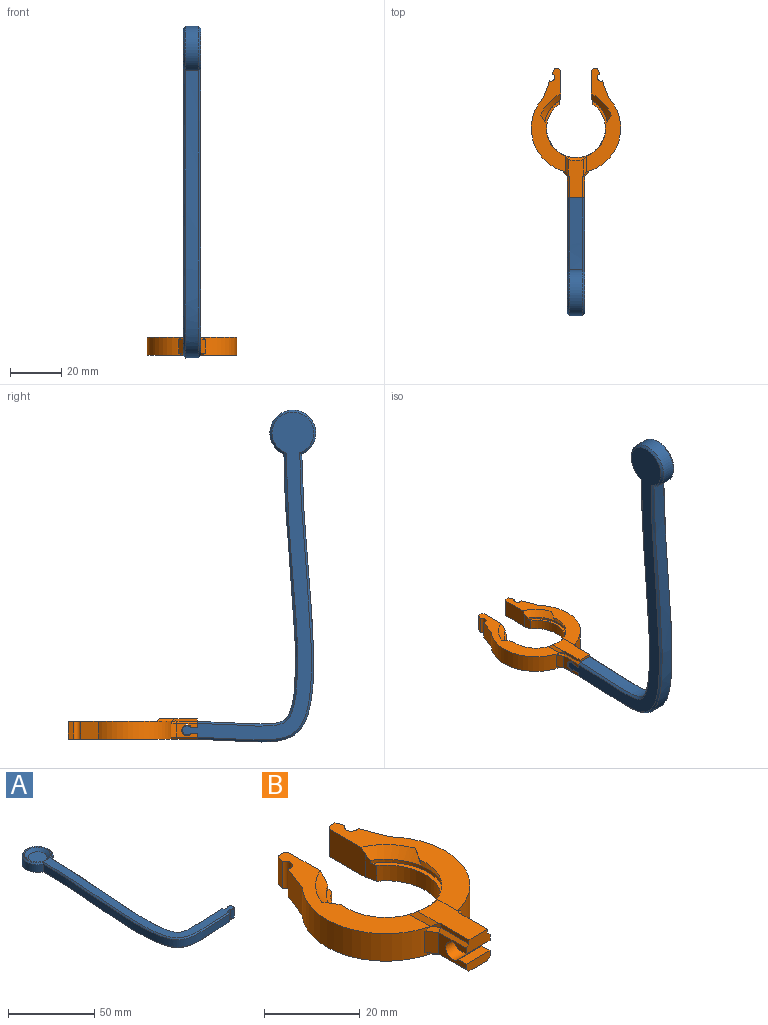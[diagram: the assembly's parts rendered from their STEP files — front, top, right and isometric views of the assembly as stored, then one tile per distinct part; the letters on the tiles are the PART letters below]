
ASSEMBLY  parts=2 mates=1
PART A: 20 faces, bbox 54x130.1x7 mm
  f0: plane 7x2.3mm, normal (1,0,0), area 15.5mm2, adj f1,f7,f8,f9,f11,f14
  f1: plane 7.01x2.67mm, normal (0,-1,0), area 16.9mm2, adj f0,f2,f8,f9,f18,f19
  f2: cylinder r=2mm len=6.6mm, axis (0,0,-1), area 65.9mm2, adj f1,f3,f18,f19
  f3: plane 7.01x2.67mm, normal (0,1,0), area 16.9mm2, adj f2,f4,f8,f9,f18,f19
  f4: plane 7x2.3mm, normal (1,0,0), area 15.5mm2, adj f3,f5,f8,f9,f10,f13
  f5: extruded ~105.77x38.57mm, area 753.8mm2, adj f4,f6,f10,f13
  f6: cylinder r=9mm len=18mm, axis (0,0,-1), area 266.5mm2, adj f5,f7,f12,f15
  f7: extruded ~112.77x45.57mm, area 813.5mm2, adj f0,f6,f11,f14
  f8: plane 128.51x51.44mm, normal (0,0,1), area 833.2mm2, adj f0,f1,f3,f4,f13,f14,f15,f17
  f9: plane 128.51x51.44mm, normal (0,0,-1), area 1004.9mm2, adj f0,f1,f3,f4,f10,f11,f12,f19
  f10: bspline ~114.19x46.54mm, area 158mm2, adj f4,f5,f9,f12
  f11: bspline ~120.82x53.15mm, area 170.1mm2, adj f0,f7,f9,f12
  f12: cone r=9mm half-angle=45deg, axis (0,0,1), area 54mm2, adj f6,f9,f10,f11
  f13: bspline ~114.2x46.55mm, area 159mm2, adj f4,f5,f8,f15
  f14: bspline ~120.83x53.16mm, area 170mm2, adj f0,f7,f8,f15
  f15: cone r=8.2mm half-angle=45deg, axis (0,0,-1), area 54mm2, adj f6,f8,f13,f14
  f16: plane 11x11mm, normal (0,0,1), area 95mm2, adj f17
  f17: cone r=5.5mm half-angle=45deg, axis (0,0,1), area 115.5mm2, adj f8,f16
  f18: cone r=1.8mm half-angle=45deg, axis (0,0,-1), area 2.6mm2, adj f1,f2,f3,f8
  f19: cone r=2mm half-angle=45deg, axis (0,0,1), area 2.6mm2, adj f1,f2,f3,f9
PART B: 56 faces, bbox 35.8x51.4x9.1 mm
  f0: plane 41.3x14.35mm, normal (0,0,1), area 206.7mm2, adj f8,f24,f25,f26,f27,f28,f30,f41
  f1: cylinder r=12.5mm len=25mm, axis (0,0,-1), area 52.2mm2, adj f6,f7,f30,f42,f43,f46,f47
  f2: plane 10.47x7.02mm, normal (-1,0,0), area 72.5mm2, adj f3,f4,f42,f45,f46
  f3: plane 41.3x14.35mm, normal (0,0,1), area 206.7mm2, adj f2,f7,f10,f11,f12,f13,f14,f40
  f4: plane 50.59x35mm, normal (0,0,-1), area 588.7mm2, adj f2,f5,f8,f10,f11,f12,f13,f14
  f5: cylinder r=11.5mm len=23mm, axis (0,0,-1), area 232.3mm2, adj f4,f6,f46,f47
  f6: plane 25x23.28mm, normal (0,0,1), area 61.7mm2, adj f1,f5,f46,f47
  f7: bspline ~14.75x12.96mm, area 49.6mm2, adj f1,f3,f30,f40,f54
  f8: plane 10.47x7.02mm, normal (1,0,0), area 72.5mm2, adj f0,f4,f43,f44,f47
  f9: plane 7x3.25mm, normal (0,-1,0), area 20.5mm2, adj f16,f17,f29,f34,f38,f49,f50,f52
  f10: cylinder r=17.5mm len=28.76mm, axis (0,0,-1), area 246.2mm2, adj f3,f4,f11,f23,f33,f35
  f11: plane 7x6.83mm, normal (0.93,0.37,0), area 51.3mm2, adj f3,f4,f10,f12
  f12: cylinder r=1.5mm len=7mm, axis (0,0,-1), area 33mm2, adj f3,f4,f11,f13
  f13: plane 7x2.1mm, normal (0.93,0.37,0), area 15.8mm2, adj f3,f4,f12,f14
  f14: plane 7x1.6mm, normal (0,1,0), area 11.2mm2, adj f3,f4,f13,f45
  f15: plane 7x2.15mm, normal (0,-1,0), area 14.4mm2, adj f4,f16,f18,f29,f32,f36
  f16: plane 8.1x5.4mm, normal (1,0,0), area 24.3mm2, adj f9,f15,f17,f18,f19,f20,f21,f22
  f17: plane 7x2.31mm, normal (0,0,-1), area 16.2mm2, adj f9,f16,f19,f29
  f18: plane 7x2.39mm, normal (0,0,1), area 16.7mm2, adj f15,f16,f20,f29
  f19: cylinder r=2.1mm len=7mm, axis (1,0,0), area 8.7mm2, adj f16,f17,f22,f29
  f20: cylinder r=2.1mm len=7mm, axis (1,0,0), area 54mm2, adj f16,f18,f21,f29
  f21: plane 7x0.7mm, normal (0,-0.6,-0.8), area 6.1mm2, adj f16,f20,f22,f29
  f22: plane 7x0.7mm, normal (0,0.6,-0.8), area 6.1mm2, adj f16,f19,f21,f29
  f23: plane 5.4x2.34mm, normal (0.81,-0.59,0), area 15.7mm2, adj f10,f16,f33,f35
  f24: cylinder r=17.5mm len=28.76mm, axis (0,0,-1), area 246.2mm2, adj f0,f4,f25,f31,f37,f39
  f25: plane 7x6.83mm, normal (-0.93,0.37,0), area 51.3mm2, adj f0,f4,f24,f26
  f26: cylinder r=1.5mm len=7mm, axis (0,0,-1), area 33mm2, adj f0,f4,f25,f27
  f27: plane 7x2.1mm, normal (-0.93,0.37,0), area 15.8mm2, adj f0,f4,f26,f28
  f28: plane 7x1.6mm, normal (0,1,0), area 11.2mm2, adj f0,f4,f27,f44
  f29: plane 8.1x5.4mm, normal (-1,0,0), area 24.3mm2, adj f9,f15,f17,f18,f19,f20,f21,f22
  f30: bspline ~14.75x12.96mm, area 48.4mm2, adj f0,f1,f7,f41,f54
  f31: plane 5.4x2.34mm, normal (-0.81,-0.59,0), area 15.7mm2, adj f24,f29,f37,f39
  f32: plane 8.37x0.8mm, normal (0.71,0,-0.71), area 9.3mm2, adj f4,f15,f16,f33
  f33: plane 2.54x2.36mm, normal (0.57,-0.42,-0.71), area 2.8mm2, adj f4,f10,f23,f32
  f34: plane 8.37x0.8mm, normal (0.71,0,0.71), area 9.3mm2, adj f9,f16,f35,f50
  f35: plane 2.54x2.36mm, normal (0.57,-0.42,0.71), area 2.8mm2, adj f10,f23,f34,f51
  f36: plane 8.37x0.8mm, normal (-0.71,0,-0.71), area 9.3mm2, adj f4,f15,f29,f37
  f37: plane 2.54x2.36mm, normal (-0.57,-0.42,-0.71), area 2.8mm2, adj f4,f24,f31,f36
  f38: plane 8.37x0.8mm, normal (-0.71,0,0.71), area 9.3mm2, adj f9,f29,f39,f49
  f39: plane 2.54x2.36mm, normal (-0.57,-0.42,0.71), area 2.8mm2, adj f24,f31,f38,f48
  f40: bspline ~3.74x3.68mm, area 4.7mm2, adj f3,f7,f42
  f41: bspline ~3.71x3.67mm, area 4.7mm2, adj f0,f30,f43
  f42: cone r=14.7mm half-angle=45deg, axis (0,0,1), area 35.9mm2, adj f1,f2,f3,f40,f46
  f43: cone r=14.7mm half-angle=45deg, axis (0,0,1), area 35.9mm2, adj f0,f1,f8,f41,f47
  f44: plane 7x0.8mm, normal (0.71,0.71,0), area 7.9mm2, adj f0,f4,f8,f28
  f45: plane 7x0.8mm, normal (-0.71,0.71,0), area 7.9mm2, adj f2,f3,f4,f14
  f46: plane 5.93x2.85mm, normal (-0.97,-0.22,0), area 13.4mm2, adj f1,f2,f4,f5,f6,f42
  f47: plane 5.93x2.85mm, normal (0.97,-0.22,0), area 13.4mm2, adj f1,f4,f5,f6,f8,f43
  f48: plane 1.74x1.28mm, normal (-0.81,-0.59,0), area 1.3mm2, adj f39,f49,f52,f55
  f49: plane 8.37x1mm, normal (-1,0,0), area 8.4mm2, adj f9,f38,f48,f52
  f50: plane 8.37x1mm, normal (1,0,0), area 8.4mm2, adj f9,f34,f51,f52
  f51: plane 1.74x1.28mm, normal (0.81,-0.59,0), area 1.3mm2, adj f35,f50,f52,f53
  f52: plane 14.87x5.95mm, normal (0,0,1), area 82.4mm2, adj f9,f48,f49,f50,f51,f53,f54,f55
  f53: plane 7.52x1.05mm, normal (0.71,0,0.71), area 8.6mm2, adj f3,f51,f52,f54
  f54: cone r=12.63mm half-angle=45deg, axis (0,0,1), area 10mm2, adj f7,f30,f52,f53,f55
  f55: plane 7.52x1.05mm, normal (-0.71,0,0.71), area 8.6mm2, adj f0,f48,f52,f54
PLACE A rot(axis=(0.58,0.58,0.58),120deg) t=(33.58,-39.99,31.69)mm
PLACE B t=(37.08,-12.85,31.69)mm fixed
MATE slider A.f2 <-> B.f19  axis (1,0,0) through (40.58,-35.99,35.19)mm
